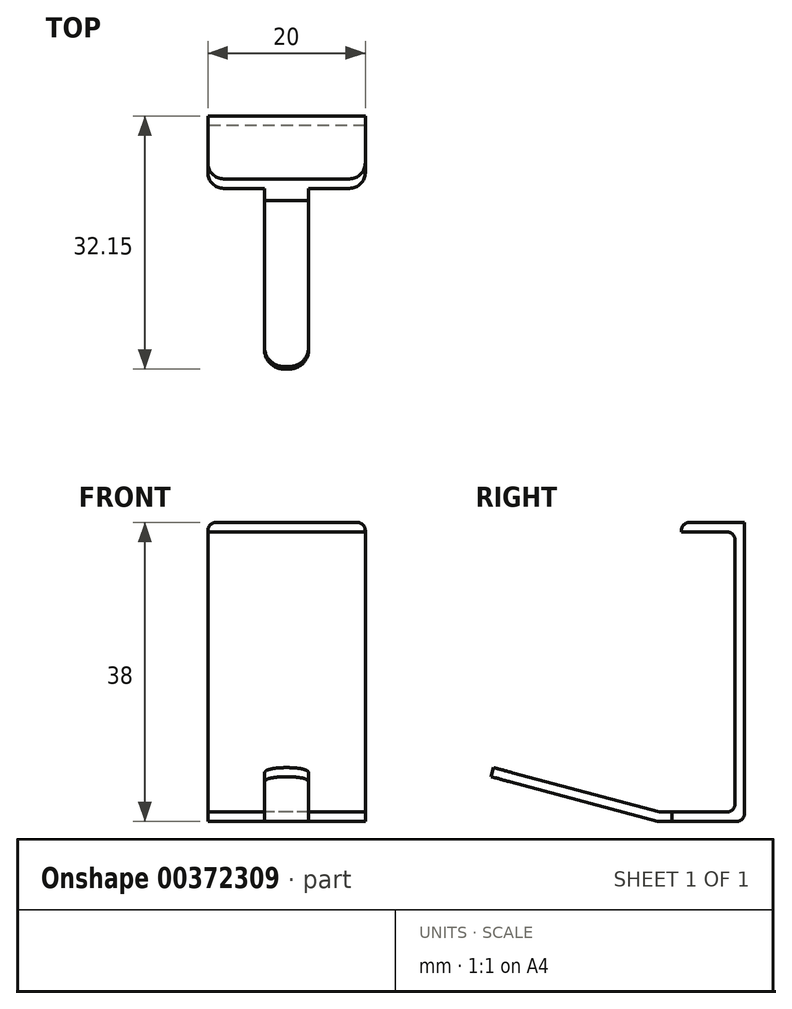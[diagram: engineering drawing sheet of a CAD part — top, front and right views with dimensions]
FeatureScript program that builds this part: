
annotation { "Feature Type Name" : "Feature", "Feature Type Description" : "" }
export const myFeature = defineFeature(function(context is Context, id is Id, definition is map)
    precondition{}
    {
        {
            var Q0;
            Q0=qCreatedBy(makeId("Right.planeOp"),FACE);
            var sketch = newSketch(context, id + "F0", { "sketchPlane" : qUnion([Q0])});
            skLineSegment(sketch, "E0.bottom", {"start": v(0, 83.02) * mm, "end": v(-1.2, 83.02) * mm});
            skLineSegment(sketch, "E0.left", {"start": v(0, 83.02) * mm, "end": v(0, 45.02) * mm});
            skLineSegment(sketch, "E0.right", {"start": v(-1.2, 83.02) * mm, "end": v(-1.2, 45.02) * mm});
            skLineSegment(sketch, "E1.bottom", {"start": v(0, 83.02) * mm, "end": v(-8, 83.02) * mm});
            skLineSegment(sketch, "E1.top", {"start": v(0, 81.82) * mm, "end": v(-8, 81.82) * mm});
            skLineSegment(sketch, "E1.left", {"start": v(0, 83.02) * mm, "end": v(0, 81.82) * mm});
            skLineSegment(sketch, "E1.right", {"start": v(-8, 83.02) * mm, "end": v(-8, 81.82) * mm});
            skLineSegment(sketch, "E2", {"start": v(-25.08, 50.06) * mm, "end": v(-10.82, 46.24) * mm});
            skLineSegment(sketch, "E3.bottom", {"start": v(-10.9, 45.02) * mm, "end": v(0, 45.02) * mm});
            skLineSegment(sketch, "E3.top", {"start": v(-10.76, 46.23) * mm, "end": v(0, 46.23) * mm});
            skLineSegment(sketch, "E3.right", {"start": v(0, 45.02) * mm, "end": v(0, 46.23) * mm});
            skLineSegment(sketch, "E4", {"start": v(-10.82, 46.24) * mm, "end": v(-10.78, 46.23) * mm});
            skLineSegment(sketch, "E5", {"start": v(-10.76, 46.23) * mm, "end": v(-10.78, 46.23) * mm});
            skLineSegment(sketch, "E6", {"start": v(-25.4, 48.9) * mm, "end": v(-32.15, 50.72) * mm});
            skLineSegment(sketch, "E7", {"start": v(-25.4, 48.9) * mm, "end": v(-10.9, 45.02) * mm});
            skLineSegment(sketch, "E8", {"start": v(-25.08, 50.06) * mm, "end": v(-31.84, 51.88) * mm});
            skLineSegment(sketch, "E9", {"start": v(-32.15, 50.72) * mm, "end": v(-31.84, 51.88) * mm});
            skSolve(sketch);
        }
        {
            var Q0;
            Q0 = qSketchRegion(id + "F0", true);
            extrude(context, id + "F1", {"entities" : qUnion([Q0]), "depth" : 20 * mm, "offsetDistance" : 25 * mm});
        }
        {
            var Q0;
            Q0=makeQuery(id+"F1.opExtrude","SWEPT_FACE",FACE,{"disambiguationData":[OSD([sQuery(id+"F0.wireOp",EDGE,"E1.bottom")])]});
            var sketch = newSketch(context, id + "F2", { "sketchPlane" : qUnion([Q0])});
            skLineSegment(sketch, "E10.bottom", {"start": v(-6.16, -9.2) * mm, "end": v(7.2, -9.2) * mm});
            skLineSegment(sketch, "E10.top", {"start": v(-6.16, -39.2) * mm, "end": v(25.71, -39.2) * mm});
            skLineSegment(sketch, "E10.left", {"start": v(-6.16, -9.2) * mm, "end": v(-6.16, -39.2) * mm});
            skLineSegment(sketch, "E10.right", {"start": v(25.71, -9.2) * mm, "end": v(25.71, -39.2) * mm});
            skPoint(sketch, "E11.middle.positionSnap0", {"position": v(10, -8) * mm});
            skPoint(sketch, "E11.centerSnap0", {"position": v(10, -8) * mm});
            skLineSegment(sketch, "E12.bottom", {"start": v(12.8, -35.15) * mm, "end": v(7.2, -35.15) * mm});
            skLineSegment(sketch, "E12.left", {"start": v(12.8, -35.15) * mm, "end": v(12.8, -9.2) * mm});
            skLineSegment(sketch, "E12.right", {"start": v(7.2, -35.15) * mm, "end": v(7.2, -9.2) * mm});
            skLineSegment(sketch, "E13.trimOffspring", {"start": v(12.8, -9.2) * mm, "end": v(25.71, -9.2) * mm});
            skSolve(sketch);
        }
        {
            var Q0;
            Q0 = qSketchRegion(id + "F2", true);
            extrude(context, id + "F3", {"entities" : qUnion([Q0]), "operationType" : NewBodyOperationType.REMOVE, "oppositeDirection" : true, "depth" : 40.4 * mm, "offsetDistance" : 25 * mm});
        }
        {
            var Q0;
            Q0=makeQuery(id+"F3.boolean.opBoolean","INTERSECT",EDGE,{"derivedFrom":[makeQuery(id+"F1.opExtrude","CAP_FACE",FACE,{"disambiguationData":[OSD([sQuery(id+"F0.wireOp",EDGE,"E0.left"),sQuery(id+"F0.wireOp",EDGE,"E0.right"),sQuery(id+"F0.wireOp",EDGE,"E1.bottom"),sQuery(id+"F0.wireOp",EDGE,"E1.top"),sQuery(id+"F0.wireOp",EDGE,"E1.left"),sQuery(id+"F0.wireOp",EDGE,"E1.right"),sQuery(id+"F0.wireOp",EDGE,"afYYLZuY-YP6R-4Ewa-z6uZ-WOQJiSGVAAqZ.left"),sQuery(id+"F0.wireOp",EDGE,"iScXeNnH-YWvK-V9rH-3Rra-Z1lrqZE27hSx.bottom"),sQuery(id+"F0.wireOp",EDGE,"iScXeNnH-YWvK-V9rH-3Rra-Z1lrqZE27hSx.top"),sQuery(id+"F0.wireOp",EDGE,"iScXeNnH-YWvK-V9rH-3Rra-Z1lrqZE27hSx.left"),sQuery(id+"F0.wireOp",EDGE,"h1KeUEKN-uQ4Q-sbFf-Wd79-6UYtKbvADJIS"),sQuery(id+"F0.wireOp",EDGE,"3OD2NNZC-d9gf-gLWn-MZg1-eH5vdrsUhXq2"),sQuery(id+"F0.wireOp",EDGE,"E2")])],"isStart":true}),makeQuery(id+"F3.opExtrude","SWEPT_FACE",FACE,{"disambiguationData":[OSD([sQuery(id+"F2.wireOp",EDGE,"E10.bottom")])]})]});
            var Q1;
            Q1=makeQuery(id+"F3.boolean.opBoolean","INTERSECT",EDGE,{"derivedFrom":[makeQuery(id+"F1.opExtrude","CAP_FACE",FACE,{"disambiguationData":[OSD([sQuery(id+"F0.wireOp",EDGE,"E0.left"),sQuery(id+"F0.wireOp",EDGE,"E0.right"),sQuery(id+"F0.wireOp",EDGE,"E1.bottom"),sQuery(id+"F0.wireOp",EDGE,"E1.top"),sQuery(id+"F0.wireOp",EDGE,"E1.left"),sQuery(id+"F0.wireOp",EDGE,"E1.right"),sQuery(id+"F0.wireOp",EDGE,"afYYLZuY-YP6R-4Ewa-z6uZ-WOQJiSGVAAqZ.left"),sQuery(id+"F0.wireOp",EDGE,"iScXeNnH-YWvK-V9rH-3Rra-Z1lrqZE27hSx.bottom"),sQuery(id+"F0.wireOp",EDGE,"iScXeNnH-YWvK-V9rH-3Rra-Z1lrqZE27hSx.top"),sQuery(id+"F0.wireOp",EDGE,"iScXeNnH-YWvK-V9rH-3Rra-Z1lrqZE27hSx.left"),sQuery(id+"F0.wireOp",EDGE,"h1KeUEKN-uQ4Q-sbFf-Wd79-6UYtKbvADJIS"),sQuery(id+"F0.wireOp",EDGE,"3OD2NNZC-d9gf-gLWn-MZg1-eH5vdrsUhXq2"),sQuery(id+"F0.wireOp",EDGE,"E2")])],"isStart":false}),makeQuery(id+"F3.opExtrude","SWEPT_FACE",FACE,{"disambiguationData":[OSD([sQuery(id+"F2.wireOp",EDGE,"E13.trimOffspring")])]})]});
            fillet(context, id + "F4", {"entities" : qUnion([Q0, Q1]), "radius" : 2 * mm, "tangentPropagation" : true, "allowEdgeOverflow" : false});
        }
        {
            var Q0;
            Q0=makeQuery(id+"F3.boolean.opBoolean","INTERSECT",EDGE,{"derivedFrom":[makeQuery(id+"F1.opExtrude","SWEPT_FACE",FACE,{"disambiguationData":[OSD([sQuery(id+"F0.wireOp",EDGE,"E9")])]}),makeQuery(id+"F3.opExtrude","SWEPT_FACE",FACE,{"disambiguationData":[OSD([sQuery(id+"F2.wireOp",EDGE,"E12.left")])]})]});
            var Q1;
            Q1=makeQuery(id+"F3.boolean.opBoolean","INTERSECT",EDGE,{"derivedFrom":[makeQuery(id+"F1.opExtrude","SWEPT_FACE",FACE,{"disambiguationData":[OSD([sQuery(id+"F0.wireOp",EDGE,"E9")])]}),makeQuery(id+"F3.opExtrude","SWEPT_FACE",FACE,{"disambiguationData":[OSD([sQuery(id+"F2.wireOp",EDGE,"E12.right")])]})]});
            fillet(context, id + "F5", {"entities" : qUnion([Q0, Q1]), "radius" : 2.5 * mm, "tangentPropagation" : true, "allowEdgeOverflow" : false});
        }
        {
            var Q0;
            Q0=makeQuery(id+"F1.opExtrude","CAP_EDGE",EDGE,{"disambiguationData":[OSD([sQuery(id+"F0.wireOp",EDGE,"E1.right")])],"isStart":false});
            var Q1;
            Q1=makeQuery(id+"F1.opExtrude","CAP_EDGE",EDGE,{"disambiguationData":[OSD([sQuery(id+"F0.wireOp",EDGE,"E1.right")])],"isStart":true});
            fillet(context, id + "F6", {"entities" : qUnion([Q0, Q1]), "radius" : 2 * mm, "allowEdgeOverflow" : false});
        }
        {
            var Q0;
            Q0=makeQuery(id+"F1.opExtrude","SWEPT_EDGE",EDGE,{"disambiguationData":[OSD([sQuery(id+"F0.wireOp",EDGE,"E0.right"),sQuery(id+"F0.wireOp",EDGE,"E3.top")])]});
            var Q1;
            Q1=makeQuery(id+"F1.opExtrude","SWEPT_EDGE",EDGE,{"disambiguationData":[OSD([sQuery(id+"F0.wireOp",EDGE,"E3.bottom"),sQuery(id+"F0.wireOp",EDGE,"E3.right")])]});
            var Q2;
            Q2=makeQuery(id+"F1.opExtrude","SWEPT_EDGE",EDGE,{"disambiguationData":[OSD([sQuery(id+"F0.wireOp",EDGE,"E1.bottom"),sQuery(id+"F0.wireOp",EDGE,"E1.left")])]});
            var Q3;
            Q3=makeQuery(id+"F1.opExtrude","SWEPT_EDGE",EDGE,{"disambiguationData":[OSD([sQuery(id+"F0.wireOp",EDGE,"E0.right"),sQuery(id+"F0.wireOp",EDGE,"E1.top")])]});
            fillet(context, id + "F7", {"entities" : qUnion([Q0, Q1, Q2, Q3]), "radius" : 1 * mm, "tangentPropagation" : true, "allowEdgeOverflow" : false});
        }
    });
